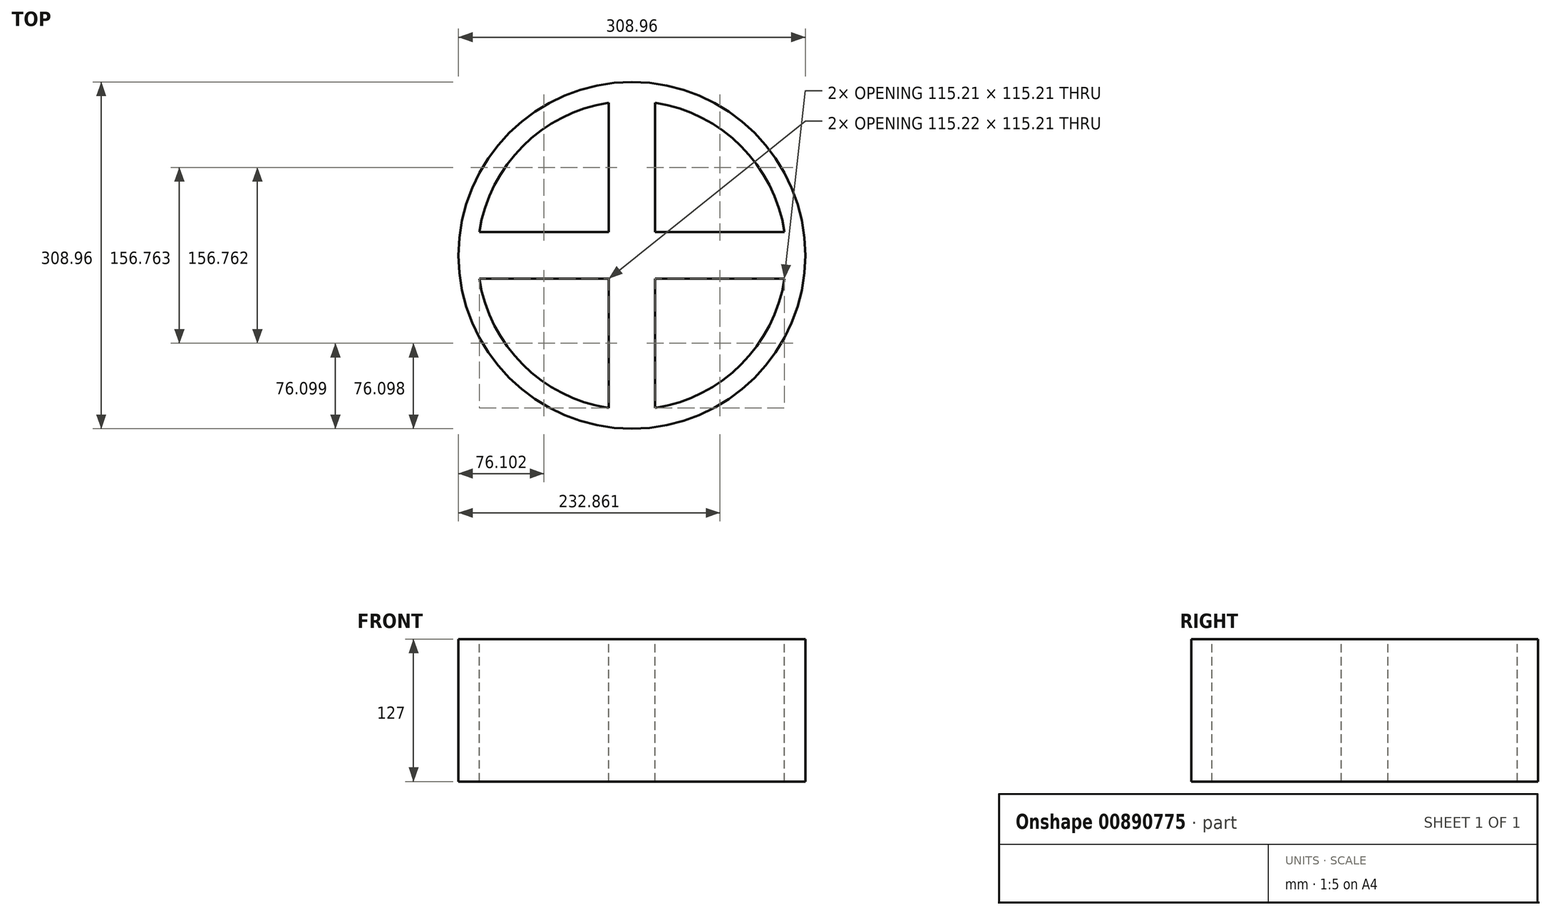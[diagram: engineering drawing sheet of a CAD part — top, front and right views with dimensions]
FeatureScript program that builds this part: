
annotation { "Feature Type Name" : "Feature", "Feature Type Description" : "" }
export const myFeature = defineFeature(function(context is Context, id is Id, definition is map)
    precondition{}
    {
        {
            var Q0;
            Q0=qCreatedBy(makeId("Top.planeOp"),FACE);
            var sketch = newSketch(context, id + "F0", { "sketchPlane" : qUnion([Q0])});
            skCircle(sketch, "E0", {"center": v(0, 0) * mm, "radius": 154.48 * mm});
            skSolve(sketch);
        }
        {
            var Q0;
            Q0=makeQuery(id+"F0.imprint","IMPRINT",FACE,{"disambiguationData":[TD([[makeQuery(id+"F0.imprint","IMPRINT",EDGE,{"derivedFrom":sQuery(id+"F0.wireOp",EDGE,"E0")}),1.0]])]});
            extrude(context, id + "F1", {"entities" : qUnion([Q0]), "depth" : 127 * mm, "offsetDistance" : 25.4 * mm});
        }
        {
            var Q0;
            Q0=makeQuery(id+"F1.opExtrude","CAP_FACE",FACE,{"disambiguationData":[OSD([sQuery(id+"F0.wireOp",EDGE,"E0")])],"isStart":false});
            var sketch = newSketch(context, id + "F2", { "sketchPlane" : qUnion([Q0])});
            skCircle(sketch, "E1", {"center": v(0, 0) * mm, "radius": 137.56 * mm});
            skLineSegment(sketch, "E2", {"start": v(0, 137.56) * mm, "end": v(0, -137.56) * mm, "construction": true});
            skLineSegment(sketch, "E3", {"start": v(-137.56, 0) * mm, "end": v(137.56, 0) * mm, "construction": true});
            skLineSegment(sketch, "E4", {"start": v(-20.77, 135.99) * mm, "end": v(-20.77, -135.99) * mm});
            skLineSegment(sketch, "E5", {"start": v(20.78, 135.98) * mm, "end": v(20.78, -135.98) * mm});
            skLineSegment(sketch, "E6", {"start": v(-135.98, 20.78) * mm, "end": v(135.98, 20.78) * mm});
            skLineSegment(sketch, "E7", {"start": v(-135.98, -20.78) * mm, "end": v(135.98, -20.78) * mm});
            skSolve(sketch);
        }
        {
            var Q0;
            {var subQ0=sQuery(id+"F2.wireOp",EDGE,"E4");var subQ1=sQuery(id+"F2.wireOp",EDGE,"E1");var subQ2=makeQuery(id+"F2.imprint","INTERSECT",VERTEX,{"disambiguationData":[OD(0.0)],"derivedFrom":[subQ1,subQ0]});Q0=makeQuery(id+"F2.imprint","IMPRINT",FACE,{"disambiguationData":[TD([[makeQuery(id+"F2.imprint","IMPRINT",EDGE,{"disambiguationData":[TD([[subQ2,-1.0]])],"derivedFrom":subQ1}),1.0]])]});}
            var Q1;
            {var subQ0=sQuery(id+"F2.wireOp",EDGE,"E5");var subQ1=sQuery(id+"F2.wireOp",EDGE,"E1");var subQ2=makeQuery(id+"F2.imprint","INTERSECT",VERTEX,{"disambiguationData":[OD(0.0)],"derivedFrom":[subQ1,subQ0]});Q1=makeQuery(id+"F2.imprint","IMPRINT",FACE,{"disambiguationData":[TD([[makeQuery(id+"F2.imprint","IMPRINT",EDGE,{"disambiguationData":[TD([[subQ2,1.0]])],"derivedFrom":subQ1}),1.0]])]});}
            var Q2;
            {var subQ0=sQuery(id+"F2.wireOp",EDGE,"E5");var subQ1=sQuery(id+"F2.wireOp",EDGE,"E1");var subQ2=makeQuery(id+"F2.imprint","INTERSECT",VERTEX,{"disambiguationData":[OD(1.0)],"derivedFrom":[subQ1,subQ0]});Q2=makeQuery(id+"F2.imprint","IMPRINT",FACE,{"disambiguationData":[TD([[makeQuery(id+"F2.imprint","IMPRINT",EDGE,{"disambiguationData":[TD([[subQ2,-1.0]])],"derivedFrom":subQ1}),1.0]])]});}
            var Q3;
            {var subQ0=sQuery(id+"F2.wireOp",EDGE,"E4");var subQ1=sQuery(id+"F2.wireOp",EDGE,"E1");var subQ2=makeQuery(id+"F2.imprint","INTERSECT",VERTEX,{"disambiguationData":[OD(1.0)],"derivedFrom":[subQ1,subQ0]});Q3=makeQuery(id+"F2.imprint","IMPRINT",FACE,{"disambiguationData":[TD([[makeQuery(id+"F2.imprint","IMPRINT",EDGE,{"disambiguationData":[TD([[subQ2,1.0]])],"derivedFrom":subQ1}),1.0]])]});}
            extrude(context, id + "F3", {"entities" : qUnion([Q0, Q1, Q2, Q3]), "operationType" : NewBodyOperationType.REMOVE, "oppositeDirection" : true, "depth" : 127 * mm, "offsetDistance" : 25.4 * mm});
        }
    });
